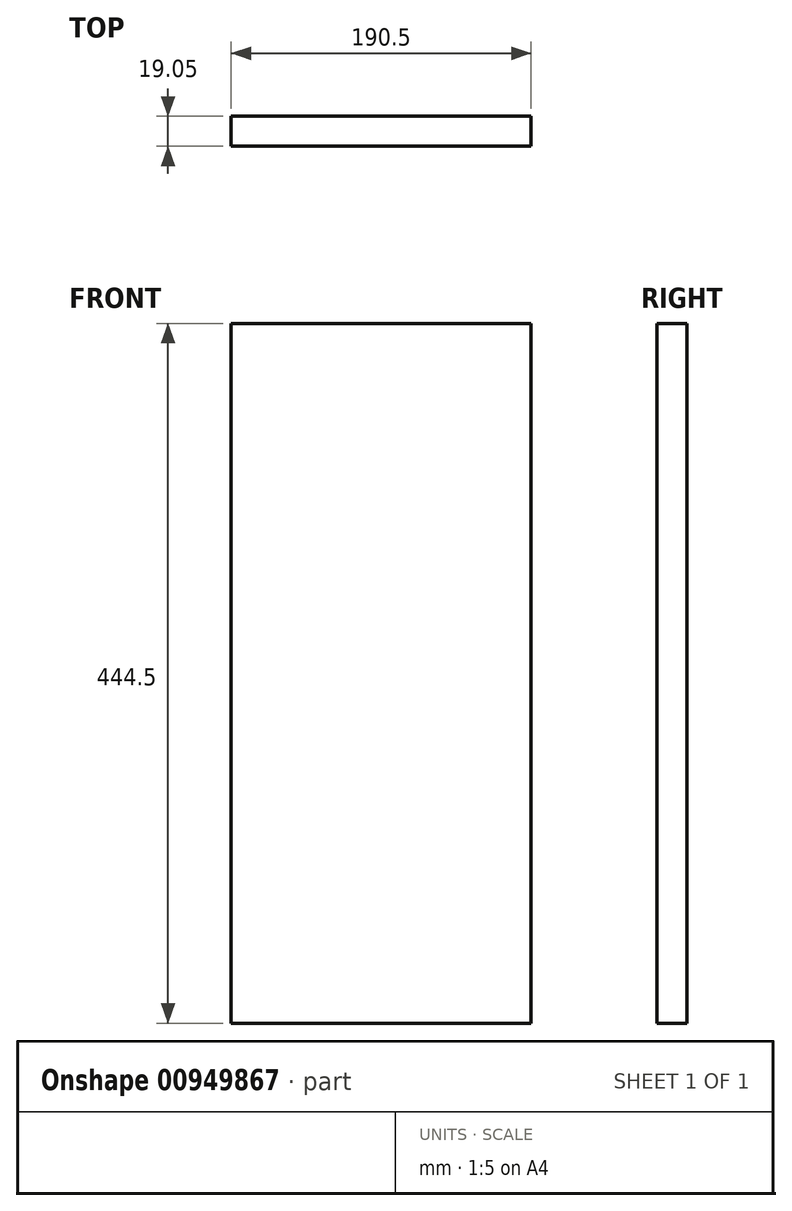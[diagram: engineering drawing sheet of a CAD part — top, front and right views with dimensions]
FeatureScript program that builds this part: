
annotation { "Feature Type Name" : "Feature", "Feature Type Description" : "" }
export const myFeature = defineFeature(function(context is Context, id is Id, definition is map)
    precondition{}
    {
        {
            var Q0;
            Q0=qCreatedBy(makeId("Front.planeOp"),FACE);
            var sketch = newSketch(context, id + "F0", { "sketchPlane" : qUnion([Q0])});
            skLineSegment(sketch, "E0.bottom", {"start": v(95.25, -222.25) * mm, "end": v(-95.25, -222.25) * mm});
            skLineSegment(sketch, "E0.top", {"start": v(95.25, 222.25) * mm, "end": v(-95.25, 222.25) * mm});
            skLineSegment(sketch, "E0.left", {"start": v(95.25, -222.25) * mm, "end": v(95.25, 222.25) * mm});
            skLineSegment(sketch, "E0.right", {"start": v(-95.25, -222.25) * mm, "end": v(-95.25, 222.25) * mm});
            skPoint(sketch, "E0.middle", {"position": v(0, 0) * mm});
            skSolve(sketch);
        }
        {
            var Q0;
            Q0 = qSketchRegion(id + "F0", true);
            extrude(context, id + "F1", {"entities" : qUnion([Q0]), "depth" : 19.05 * mm, "offsetDistance" : 25.4 * mm});
        }
    });
